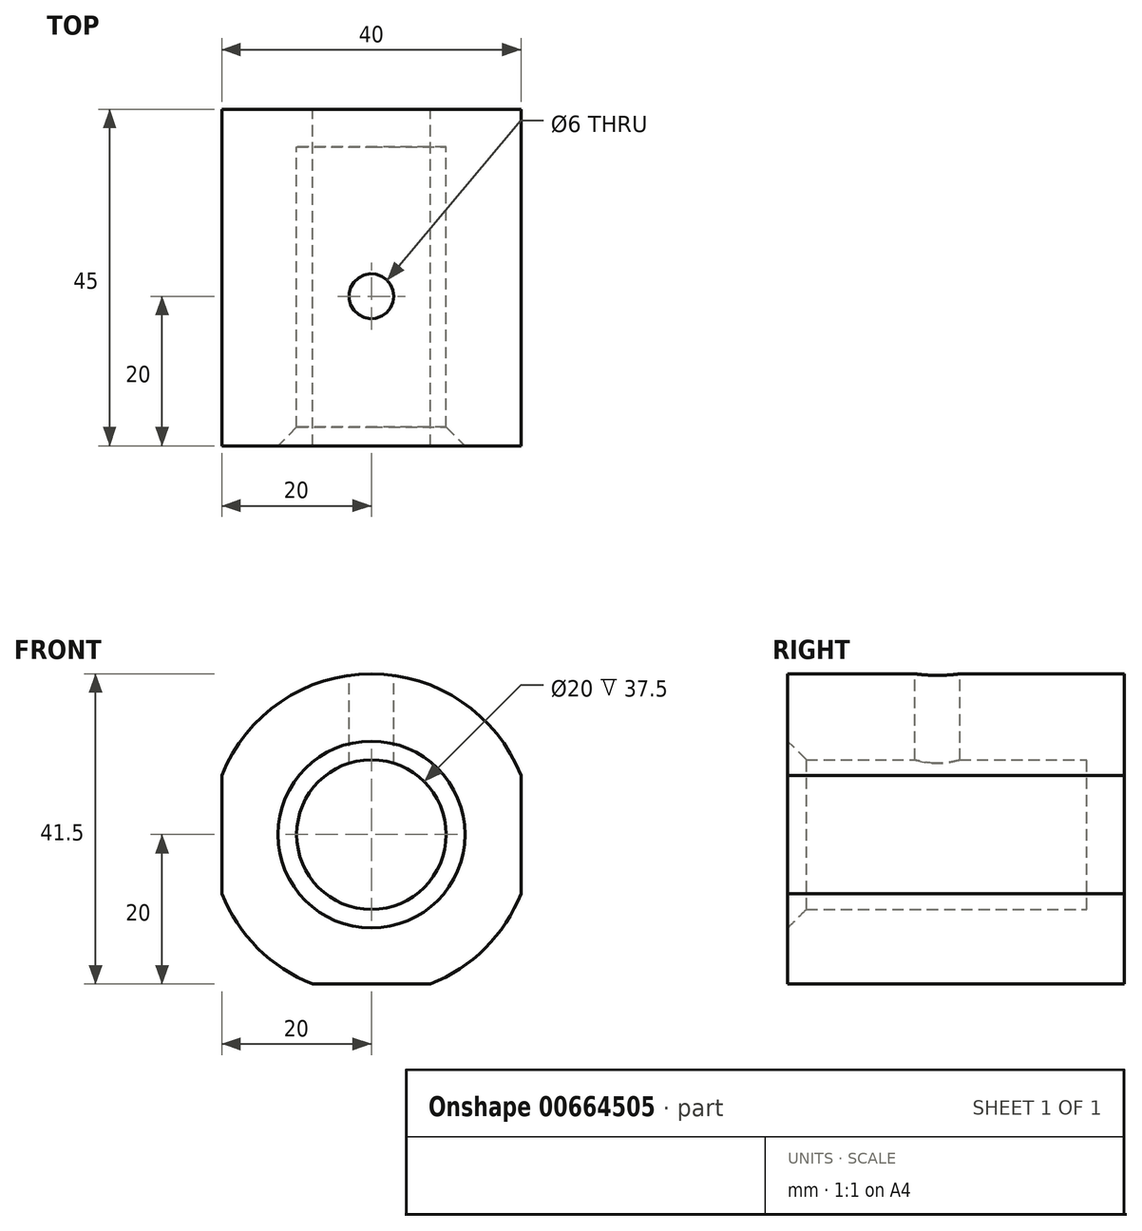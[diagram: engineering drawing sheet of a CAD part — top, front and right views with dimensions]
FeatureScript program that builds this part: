
annotation { "Feature Type Name" : "Feature", "Feature Type Description" : "" }
export const myFeature = defineFeature(function(context is Context, id is Id, definition is map)
    precondition{}
    {
        {
            var Q0;
            Q0=qCreatedBy(makeId("Front.planeOp"),FACE);
            var sketch = newSketch(context, id + "F0", { "sketchPlane" : qUnion([Q0])});
            skCircle(sketch, "E0", {"center": v(0, 0) * mm, "radius": 21.5 * mm});
            skCircle(sketch, "E1", {"center": v(0, 0) * mm, "radius": 10 * mm});
            skLineSegment(sketch, "E2", {"start": v(0, 0) * mm, "end": v(0, -20) * mm});
            skLineSegment(sketch, "E3", {"start": v(0, 0) * mm, "end": v(20, 0) * mm});
            skLineSegment(sketch, "E4", {"start": v(0, 0) * mm, "end": v(-20, 0) * mm});
            skLineSegment(sketch, "E5", {"start": v(-20, 7.89) * mm, "end": v(-20, -7.89) * mm});
            skLineSegment(sketch, "E6", {"start": v(-7.89, -20) * mm, "end": v(7.89, -20) * mm});
            skLineSegment(sketch, "E7", {"start": v(20, -7.89) * mm, "end": v(20, 7.89) * mm});
            skSolve(sketch);
        }
        {
            var Q0;
            {var subQ0=sQuery(id+"F0.wireOp",EDGE,"E5");var subQ9=sQuery(id+"F0.wireOp",EDGE,"E0");var subQ10=makeQuery(id+"F0.imprint","INTERSECT",VERTEX,{"disambiguationData":[OD(1.0)],"derivedFrom":[subQ9,subQ0]});Q0=makeQuery(id+"F0.imprint","IMPRINT",FACE,{"disambiguationData":[TD([[makeQuery(id+"F0.imprint","IMPRINT",EDGE,{"disambiguationData":[TD([[subQ10,-1.0]])],"derivedFrom":subQ9}),1.0]])]});}
            var Q1;
            {var subQ5=sQuery(id+"F0.wireOp",EDGE,"E6");var subQ9=sQuery(id+"F0.wireOp",EDGE,"E0");var subQ11=makeQuery(id+"F0.imprint","INTERSECT",VERTEX,{"disambiguationData":[OD(1.0)],"derivedFrom":[subQ9,subQ5]});Q1=makeQuery(id+"F0.imprint","IMPRINT",FACE,{"disambiguationData":[TD([[makeQuery(id+"F0.imprint","IMPRINT",EDGE,{"disambiguationData":[TD([[subQ11,-1.0]])],"derivedFrom":subQ9}),1.0]])]});}
            var Q2;
            {var subQ0=sQuery(id+"F0.wireOp",EDGE,"E5");var subQ9=sQuery(id+"F0.wireOp",EDGE,"E0");var subQ10=makeQuery(id+"F0.imprint","INTERSECT",VERTEX,{"disambiguationData":[OD(0.0)],"derivedFrom":[subQ9,subQ0]});Q2=makeQuery(id+"F0.imprint","IMPRINT",FACE,{"disambiguationData":[TD([[makeQuery(id+"F0.imprint","IMPRINT",EDGE,{"disambiguationData":[TD([[subQ10,1.0]])],"derivedFrom":subQ9}),1.0]])]});}
            extrude(context, id + "F1", {"entities" : qUnion([Q0, Q1, Q2]), "depth" : 40 * mm, "offsetDistance" : 25 * mm});
        }
        {
            var Q0;
            Q0=makeQuery(id+"F1.opExtrude","CAP_FACE",FACE,{"disambiguationData":[OSD([sQuery(id+"F0.wireOp",EDGE,"E0"),sQuery(id+"F0.wireOp",EDGE,"E1"),sQuery(id+"F0.wireOp",EDGE,"E5"),sQuery(id+"F0.wireOp",EDGE,"E6"),sQuery(id+"F0.wireOp",EDGE,"E7")])],"isStart":true});
            var sketch = newSketch(context, id + "F2", { "sketchPlane" : qUnion([Q0])});
            skLineSegment(sketch, "E8", {"start": v(-20, 7.89) * mm, "end": v(-20, -7.89) * mm});
            skLineSegment(sketch, "E9", {"start": v(20, -7.89) * mm, "end": v(20, 7.89) * mm});
            skLineSegment(sketch, "E10", {"start": v(7.89, -20) * mm, "end": v(-7.89, -20) * mm});
            skCircle(sketch, "E11", {"center": v(0, 0) * mm, "radius": 21.5 * mm});
            skSolve(sketch);
        }
        {
            var Q0;
            Q0=makeQuery(id+"F2.imprint","IMPRINT",FACE,{"disambiguationData":[TD([[makeQuery(id+"F2.imprint","IMPRINT",EDGE,{"derivedFrom":makeQuery(id+"F1.opExtrude","CAP_EDGE",EDGE,{"disambiguationData":[OSD([sQuery(id+"F0.wireOp",EDGE,"E1")])],"isStart":true})}),-1.0]])]});
            var Q1;
            {var subQ2=sQuery(id+"F2.wireOp",EDGE,"E8");Q1=makeQuery(id+"F2.imprint","IMPRINT",FACE,{"disambiguationData":[TD([[makeQuery(id+"F2.imprint","IMPRINT",EDGE,{"derivedFrom":subQ2}),-1.0]])]});}
            extrude(context, id + "F3", {"entities" : qUnion([Q0, Q1]), "operationType" : NewBodyOperationType.ADD, "depth" : 5 * mm, "offsetDistance" : 25 * mm});
        }
        {
            var Q0;
            Q0=qCreatedBy(makeId("Top.planeOp"),FACE);
            cPlane(context, id + "F4", {"entities" : qUnion([Q0]), "cplaneType" : CPlaneType.OFFSET, "offset" : 21.5 * mm, "width" : 150 * mm, "height" : 150 * mm});
        }
        {
            var Q0;
            Q0=qCreatedBy(id+"F4.planeOp",FACE);
            var sketch = newSketch(context, id + "F5", { "sketchPlane" : qUnion([Q0])});
            skLineSegment(sketch, "E12", {"start": v(0, 0) * mm, "end": v(0, -20) * mm});
            skCircle(sketch, "E13", {"center": v(0, -20) * mm, "radius": 3 * mm});
            skSolve(sketch);
        }
        {
            var Q0;
            Q0=makeQuery(id+"F5.imprint","IMPRINT",FACE,{"disambiguationData":[TD([[makeQuery(id+"F5.imprint","IMPRINT",EDGE,{"derivedFrom":sQuery(id+"F5.wireOp",EDGE,"E13")}),1.0]])]});
            extrude(context, id + "F6", {"entities" : qUnion([Q0]), "operationType" : NewBodyOperationType.REMOVE, "oppositeDirection" : true, "depth" : 15 * mm, "offsetDistance" : 25 * mm});
        }
        {
            var Q0;
            Q0=makeQuery(id+"F1.opExtrude","CAP_EDGE",EDGE,{"disambiguationData":[OSD([sQuery(id+"F0.wireOp",EDGE,"E1")])],"isStart":false});
            chamfer(context, id + "F7", {"entities" : qUnion([Q0]), "width" : 2.5 * mm, "tangentPropagation" : true});
        }
    });
